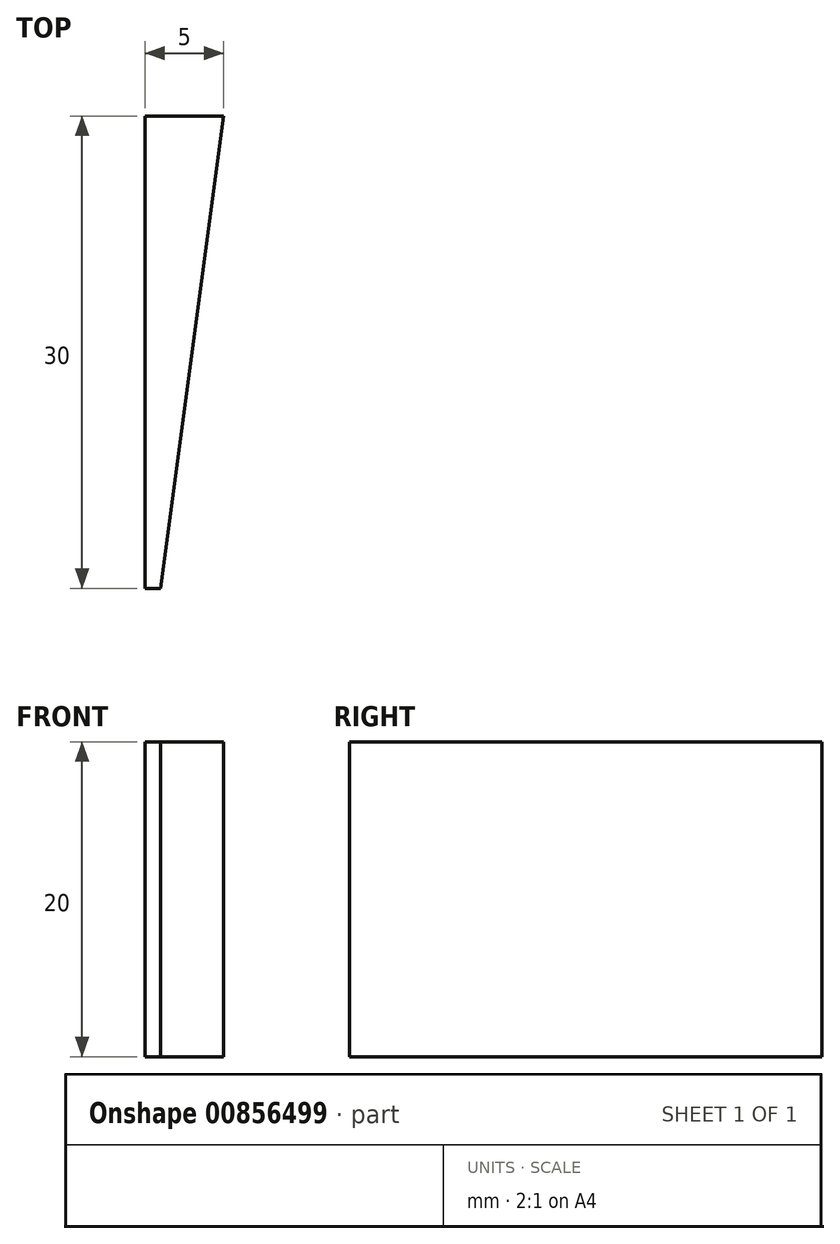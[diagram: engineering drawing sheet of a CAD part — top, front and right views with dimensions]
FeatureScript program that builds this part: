
annotation { "Feature Type Name" : "Feature", "Feature Type Description" : "" }
export const myFeature = defineFeature(function(context is Context, id is Id, definition is map)
    precondition{}
    {
        {
            var Q0;
            Q0=qCreatedBy(makeId("Top.planeOp"),FACE);
            var sketch = newSketch(context, id + "F0", { "sketchPlane" : qUnion([Q0])});
            skLineSegment(sketch, "E0", {"start": v(0, 0) * mm, "end": v(0, -30) * mm});
            skLineSegment(sketch, "E1", {"start": v(0, 0) * mm, "end": v(5, 0) * mm});
            skLineSegment(sketch, "E2", {"start": v(5, 0) * mm, "end": v(1, -30) * mm});
            skLineSegment(sketch, "E3", {"start": v(0, -30) * mm, "end": v(1, -30) * mm});
            skSolve(sketch);
        }
        {
            var Q0;
            Q0=makeQuery(id+"F0.imprint","IMPRINT",FACE,{"disambiguationData":[TD([[makeQuery(id+"F0.imprint","IMPRINT",EDGE,{"derivedFrom":sQuery(id+"F0.wireOp",EDGE,"E0")}),1.0]])]});
            extrude(context, id + "F1", {"entities" : qUnion([Q0]), "depth" : 20 * mm, "offsetDistance" : 25 * mm});
        }
    });
